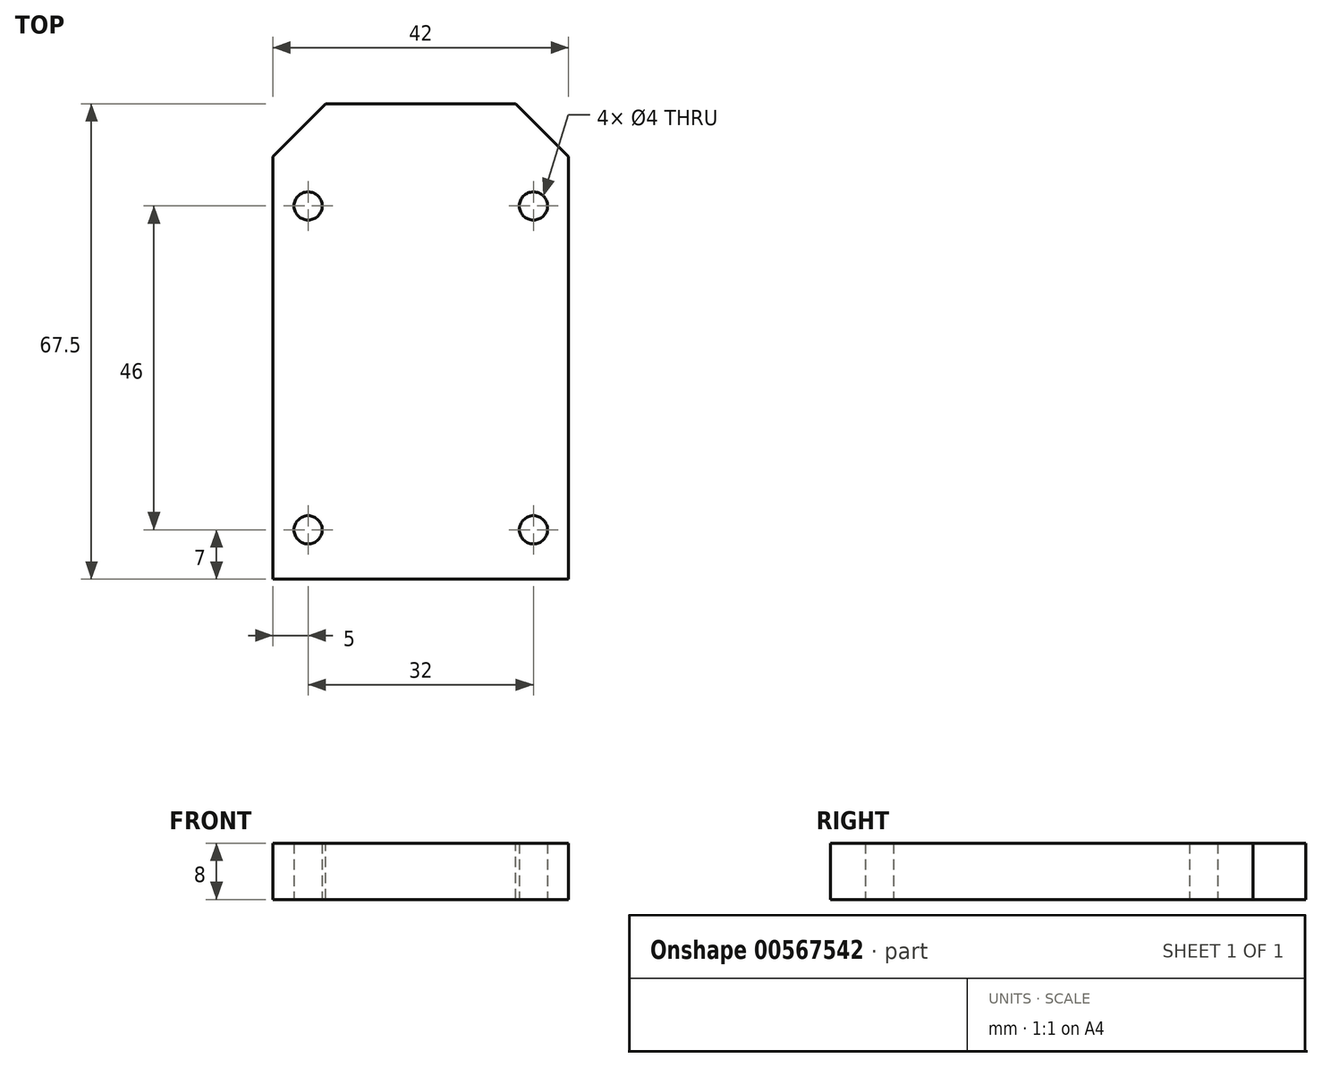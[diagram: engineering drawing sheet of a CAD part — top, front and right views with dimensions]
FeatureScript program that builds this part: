
annotation { "Feature Type Name" : "Feature", "Feature Type Description" : "" }
export const myFeature = defineFeature(function(context is Context, id is Id, definition is map)
    precondition{}
    {
        {
            var Q0;
            Q0=qCreatedBy(makeId("Top.planeOp"),FACE);
            var sketch = newSketch(context, id + "F0", { "sketchPlane" : qUnion([Q0])});
            skLineSegment(sketch, "E0.bottom", {"start": v(21, -30) * mm, "end": v(-21, -30) * mm});
            skLineSegment(sketch, "E0.top", {"start": v(21, 30) * mm, "end": v(-21, 30) * mm});
            skLineSegment(sketch, "E0.left", {"start": v(21, -30) * mm, "end": v(21, 30) * mm});
            skLineSegment(sketch, "E0.right", {"start": v(-21, -30) * mm, "end": v(-21, 30) * mm});
            skPoint(sketch, "E0.middle", {"position": v(0, 0) * mm});
            skCircle(sketch, "E1", {"center": v(-16, 23) * mm, "radius": 2 * mm});
            skCircle(sketch, "E2.MirrorC", {"center": v(16, 23) * mm, "radius": 2 * mm});
            skCircle(sketch, "E3.MirrorC", {"center": v(-16, -23) * mm, "radius": 2 * mm});
            skCircle(sketch, "E4.MirrorC", {"center": v(16, -23) * mm, "radius": 2 * mm});
            skSolve(sketch);
        }
        {
            var Q0;
            Q0=makeQuery(id+"F0.imprint","IMPRINT",FACE,{"disambiguationData":[TD([[makeQuery(id+"F0.imprint","IMPRINT",EDGE,{"derivedFrom":sQuery(id+"F0.wireOp",EDGE,"E0.bottom")}),-1.0]])]});
            extrude(context, id + "F1", {"entities" : qUnion([Q0]), "depth" : 8 * mm, "offsetDistance" : 25 * mm});
        }
        {
            var Q0;
            Q0=makeQuery(id+"F1.opExtrude","CAP_FACE",FACE,{"disambiguationData":[OSD([sQuery(id+"F0.wireOp",EDGE,"E0.bottom"),sQuery(id+"F0.wireOp",EDGE,"E0.top"),sQuery(id+"F0.wireOp",EDGE,"E0.left"),sQuery(id+"F0.wireOp",EDGE,"E0.right"),sQuery(id+"F0.wireOp",EDGE,"E1"),sQuery(id+"F0.wireOp",EDGE,"E2.MirrorC"),sQuery(id+"F0.wireOp",EDGE,"E3.MirrorC"),sQuery(id+"F0.wireOp",EDGE,"E4.MirrorC")])],"isStart":false});
            var sketch = newSketch(context, id + "F2", { "sketchPlane" : qUnion([Q0])});
            skLineSegment(sketch, "E5", {"start": v(-21, 30) * mm, "end": v(-13.5, 37.5) * mm});
            skLineSegment(sketch, "E6", {"start": v(-13.5, 37.5) * mm, "end": v(13.5, 37.5) * mm});
            skLineSegment(sketch, "E7", {"start": v(13.5, 37.5) * mm, "end": v(21, 30) * mm});
            skLineSegment(sketch, "E8", {"start": v(21, 30) * mm, "end": v(-21, 30) * mm});
            skSolve(sketch);
        }
        {
            var Q0;
            Q0 = qSketchRegion(id + "F2", true);
            extrude(context, id + "F3", {"entities" : qUnion([Q0]), "operationType" : NewBodyOperationType.ADD, "oppositeDirection" : true, "depth" : 8 * mm, "offsetDistance" : 25 * mm});
        }
    });
